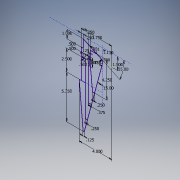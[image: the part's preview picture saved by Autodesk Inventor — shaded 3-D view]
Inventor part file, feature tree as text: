
AUTODESK INVENTOR PART (.ipt)
format: ipt  version: 2017 SP1 (Build 210196100, 196)  size: 122,368 bytes
history: native  units: in
note: dims shown in document units (in); Inventor stores cm internally (conversion verified against a paired STEP export)
features: sketch x1
ambient origin geometry x8: Origin, YZ Plane, XZ Plane, XY Plane, X Axis, Y Axis, Z Axis, Center Point
feature tree (1):
  sketch  "Sketch1"  dims[d0=0.5in d1=1.13in d3=15.0deg d4=0.25in d9=1.5in d11=0.5in d13=3.75in d14=0.25in d15=1.0in d16=0.25in d17=0.5in d18=0.234in d19=0.234in d20=0.5in d22=4.25in d23=2.5in d25=1.0in d26=0.25in d27=5.25in d28=0.125in d29=4.0in d30=0.25in d31=0.1718in d32=1.75in d33=0.125in d34=0.801in d35=0.375in]
